# Revit family: NLRS_57_DUF_UN_instortkanaal-rechthoekig-verloop_LT_velu
name_source: partatom
category: Duct Fittings
units: mm (PartAtom-declared; Revit-internal decimal feet)

## family parameters
Always vertical = Yes
Cut with Voids When Loaded = No
Part Type = Transition
Round Connector Dimension = Use Diameter
Shared = No
Work Plane-Based = No

## types (1)
- Verloop Rechthoekig
    Assembly Code = 57.00
    Default Elevation = 0 mm  [stored 0 ft]
    Description = VELU Instort Kanaal: rechthoekig verloop
    Manufacturer = Velu Klimaattechnische Groothandel
    Model = VIK rechthoekig verloop
    NLRS_C_content_datum_gewijzigd = 18-01-2023
    NLRS_C_content_provider = Velu Klimaattechnische Groothandel
    NLRS_C_content_versie = 3.20.00
    NLRS_C_description = VELU Instort Kanaal: rechthoekig verloop
    Type Comments = Enkel geschikt voor VELU instort kanaal maten
    URL = https://webshop.velu.nl
    VELU_Article_Data = RHV
    VELU_Centerline = Yes

note: [stored X ft] marks values corroborated as IEEE doubles in the binary element streams (Revit-internal decimal feet)

## geometry (parser evidence)
native form markers: Sweep x4
no freeform markers — native parametric forms only
